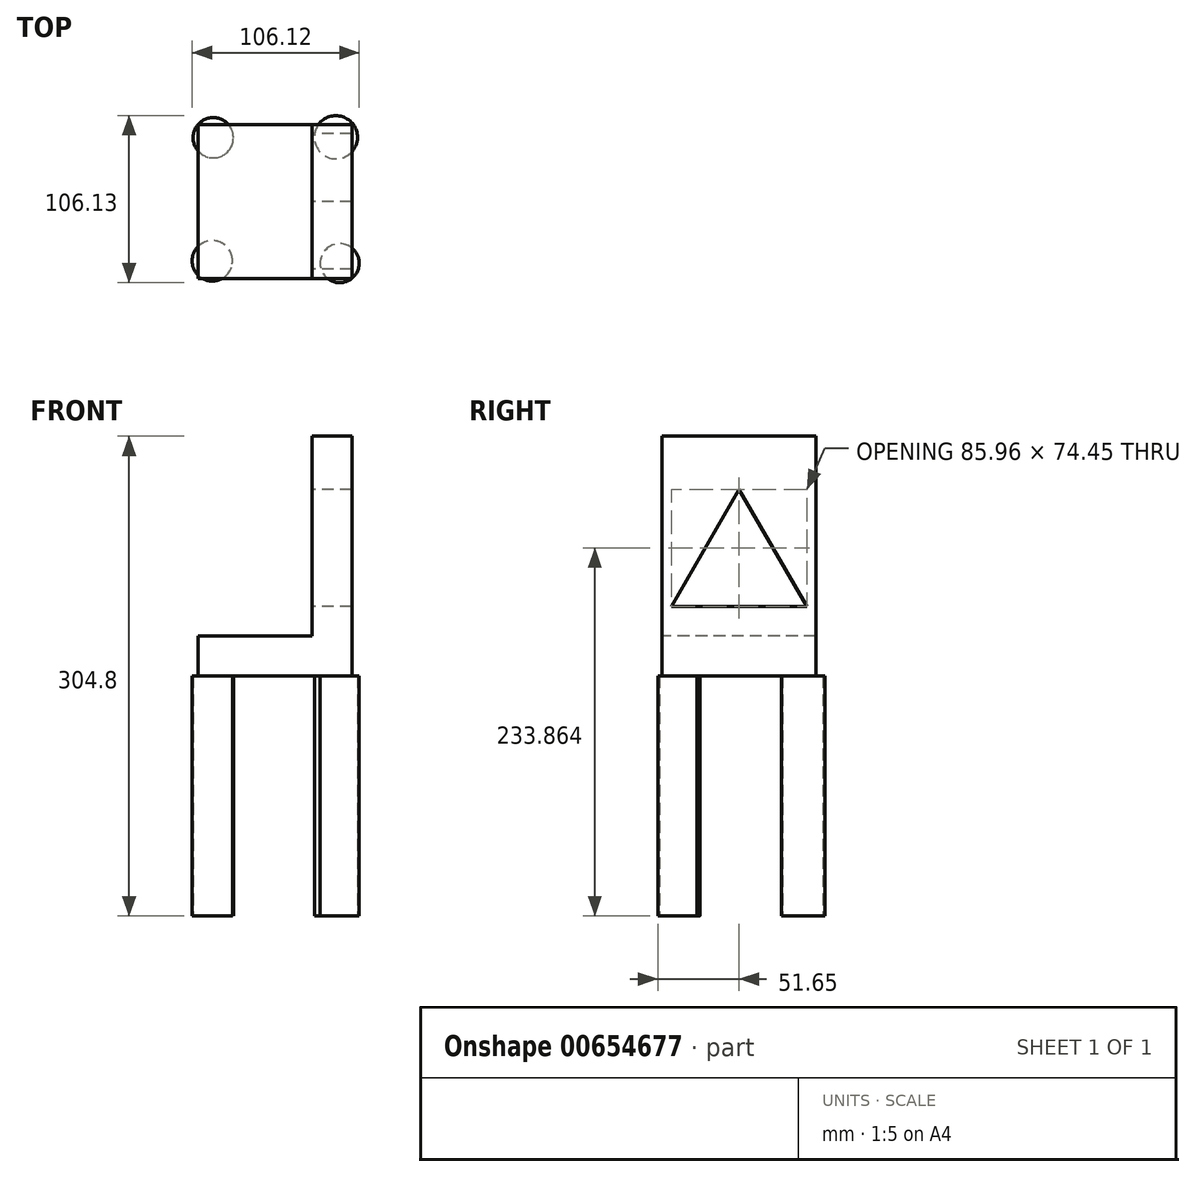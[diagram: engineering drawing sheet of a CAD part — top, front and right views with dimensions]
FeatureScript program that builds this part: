
annotation { "Feature Type Name" : "Feature", "Feature Type Description" : "" }
export const myFeature = defineFeature(function(context is Context, id is Id, definition is map)
    precondition{}
    {
        {
            var Q0;
            Q0=qCreatedBy(makeId("Top.planeOp"),FACE);
            var sketch = newSketch(context, id + "F0", { "sketchPlane" : qUnion([Q0])});
            skCircle(sketch, "E0", {"center": v(-38.35, 40.46) * mm, "radius": 12.79 * mm});
            skCircle(sketch, "E1", {"center": v(39.55, 40.76) * mm, "radius": 13.72 * mm});
            skCircle(sketch, "E2", {"center": v(-38.95, -37.75) * mm, "radius": 12.8 * mm});
            skCircle(sketch, "E3", {"center": v(41.96, -39.25) * mm, "radius": 12.4 * mm});
            skSolve(sketch);
        }
        {
            var Q0;
            Q0 = qSketchRegion(id + "F0", true);
            extrude(context, id + "F1", {"entities" : qUnion([Q0]), "depth" : 152.4 * mm, "offsetDistance" : 25.4 * mm});
        }
        {
            var Q0;
            Q0=makeQuery(id+"F1.opExtrude","CAP_FACE",FACE,{"disambiguationData":[OSD([sQuery(id+"F0.wireOp",EDGE,"E3")])],"isStart":false});
            var sketch = newSketch(context, id + "F2", { "sketchPlane" : qUnion([Q0])});
            skLineSegment(sketch, "E4.bottom", {"start": v(49.68, -48.96) * mm, "end": v(-47.82, -48.96) * mm});
            skLineSegment(sketch, "E4.top", {"start": v(49.68, 48.85) * mm, "end": v(-47.82, 48.85) * mm});
            skLineSegment(sketch, "E4.left", {"start": v(49.68, -48.96) * mm, "end": v(49.68, 48.85) * mm});
            skLineSegment(sketch, "E4.right", {"start": v(-47.82, -48.96) * mm, "end": v(-47.82, 48.85) * mm});
            skSolve(sketch);
        }
        {
            var Q0;
            Q0 = qSketchRegion(id + "F2", true);
            extrude(context, id + "F3", {"entities" : qUnion([Q0]), "depth" : 25.4 * mm, "offsetDistance" : 25.4 * mm});
        }
        {
            var Q0;
            Q0=makeQuery(id+"F3.opExtrude","CAP_FACE",FACE,{"disambiguationData":[OSD([sQuery(id+"F2.wireOp",EDGE,"E4.bottom"),sQuery(id+"F2.wireOp",EDGE,"E4.top"),sQuery(id+"F2.wireOp",EDGE,"E4.left"),sQuery(id+"F2.wireOp",EDGE,"E4.right")])],"isStart":false});
            var sketch = newSketch(context, id + "F4", { "sketchPlane" : qUnion([Q0])});
            skLineSegment(sketch, "E5.bottom", {"start": v(49.68, 48.85) * mm, "end": v(24.46, 48.85) * mm});
            skLineSegment(sketch, "E5.top", {"start": v(49.68, -48.96) * mm, "end": v(24.46, -48.96) * mm});
            skLineSegment(sketch, "E5.left", {"start": v(49.68, 48.85) * mm, "end": v(49.68, -48.96) * mm});
            skLineSegment(sketch, "E5.right", {"start": v(24.46, 48.85) * mm, "end": v(24.46, -48.96) * mm});
            skSolve(sketch);
        }
        {
            var Q0;
            Q0 = qSketchRegion(id + "F4", true);
            extrude(context, id + "F5", {"entities" : qUnion([Q0]), "operationType" : NewBodyOperationType.ADD, "depth" : 127 * mm, "offsetDistance" : 25.4 * mm});
        }
        {
            var Q0;
            Q0=makeQuery(id+"F5.opExtrude","SWEPT_FACE",FACE,{"disambiguationData":[OSD([sQuery(id+"F4.wireOp",EDGE,"E5.right")])]});
            var sketch = newSketch(context, id + "F6", { "sketchPlane" : qUnion([Q0])});
            skCircle(sketch, "E6.cCircle", {"center": v(0, 221.46) * mm, "radius": 24.82 * mm, "construction": true});
            skLineSegment(sketch, "E6.0", {"start": v(42.98, 196.64) * mm, "end": v(-42.98, 196.64) * mm});
            skLineSegment(sketch, "E6.1", {"start": v(-42.98, 196.64) * mm, "end": v(0, 271.09) * mm});
            skLineSegment(sketch, "E6.2", {"start": v(0, 271.09) * mm, "end": v(42.98, 196.64) * mm});
            skPoint(sketch, "E6.0.midPoint", {"position": v(0, 196.64) * mm});
            skSolve(sketch);
        }
        {
            var Q0;
            Q0 = qSketchRegion(id + "F6", true);
            extrude(context, id + "F7", {"entities" : qUnion([Q0]), "operationType" : NewBodyOperationType.REMOVE, "oppositeDirection" : true, "depth" : 76.2 * mm, "offsetDistance" : 25.4 * mm});
        }
    });
